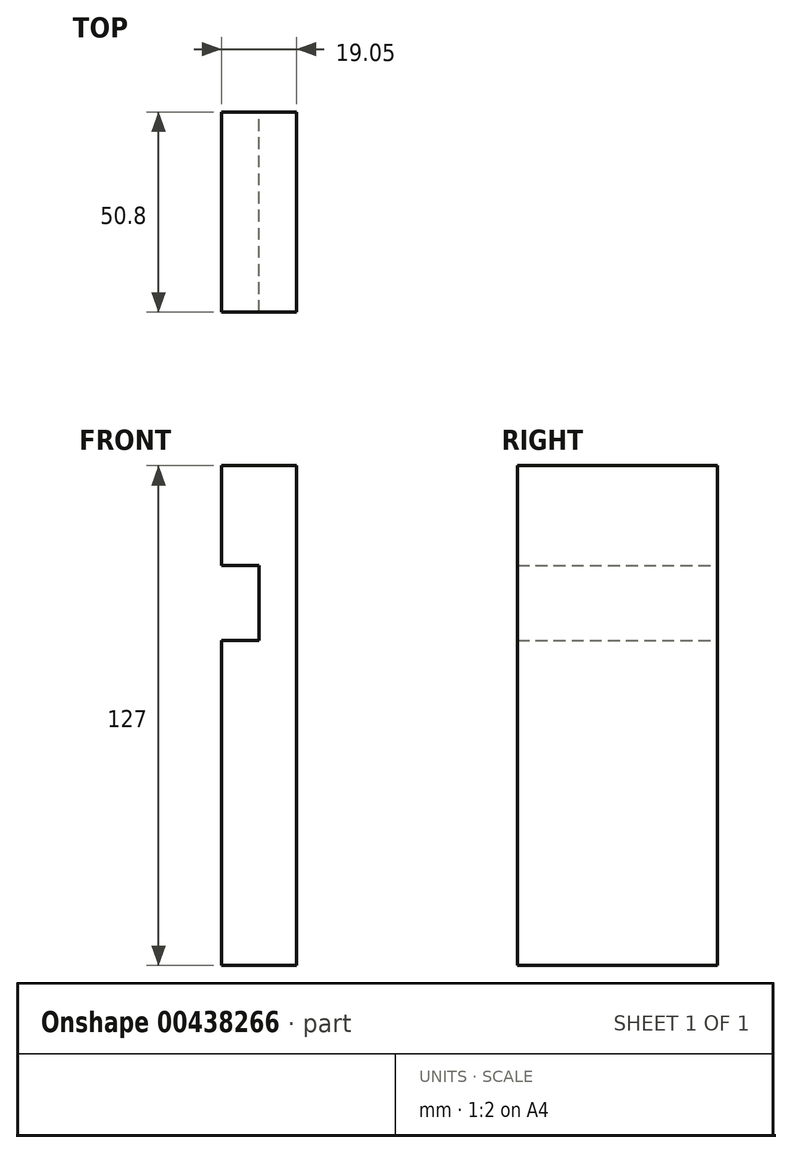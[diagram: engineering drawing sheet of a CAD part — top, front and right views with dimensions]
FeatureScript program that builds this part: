
annotation { "Feature Type Name" : "Feature", "Feature Type Description" : "" }
export const myFeature = defineFeature(function(context is Context, id is Id, definition is map)
    precondition{}
    {
        {
            var Q0;
            Q0=qCreatedBy(makeId("Front.planeOp"),FACE);
            var sketch = newSketch(context, id + "F0", { "sketchPlane" : qUnion([Q0])});
            skLineSegment(sketch, "E0", {"start": v(1.2, 106.65) * mm, "end": v(1.2, -20.35) * mm});
            skLineSegment(sketch, "E1", {"start": v(1.2, 106.65) * mm, "end": v(-17.84, 106.65) * mm});
            skLineSegment(sketch, "E2", {"start": v(-17.84, 106.65) * mm, "end": v(-17.84, 81.25) * mm});
            skLineSegment(sketch, "E3", {"start": v(-17.84, 81.25) * mm, "end": v(-8.32, 81.25) * mm});
            skLineSegment(sketch, "E4", {"start": v(-8.32, 81.25) * mm, "end": v(-8.32, 62.2) * mm});
            skLineSegment(sketch, "E5", {"start": v(-8.32, 62.2) * mm, "end": v(-17.84, 62.2) * mm});
            skLineSegment(sketch, "E6", {"start": v(-17.84, 62.2) * mm, "end": v(-17.84, -20.35) * mm});
            skLineSegment(sketch, "E7", {"start": v(-17.84, -20.35) * mm, "end": v(1.2, -20.35) * mm});
            skSolve(sketch);
        }
        {
            var Q0;
            Q0=makeQuery(id+"F0.imprint","IMPRINT",FACE,{"disambiguationData":[TD([[makeQuery(id+"F0.imprint","IMPRINT",EDGE,{"derivedFrom":sQuery(id+"F0.wireOp",EDGE,"E0")}),-1.0]])]});
            extrude(context, id + "F1", {"entities" : qUnion([Q0]), "depth" : 50.8 * mm});
        }
    });
